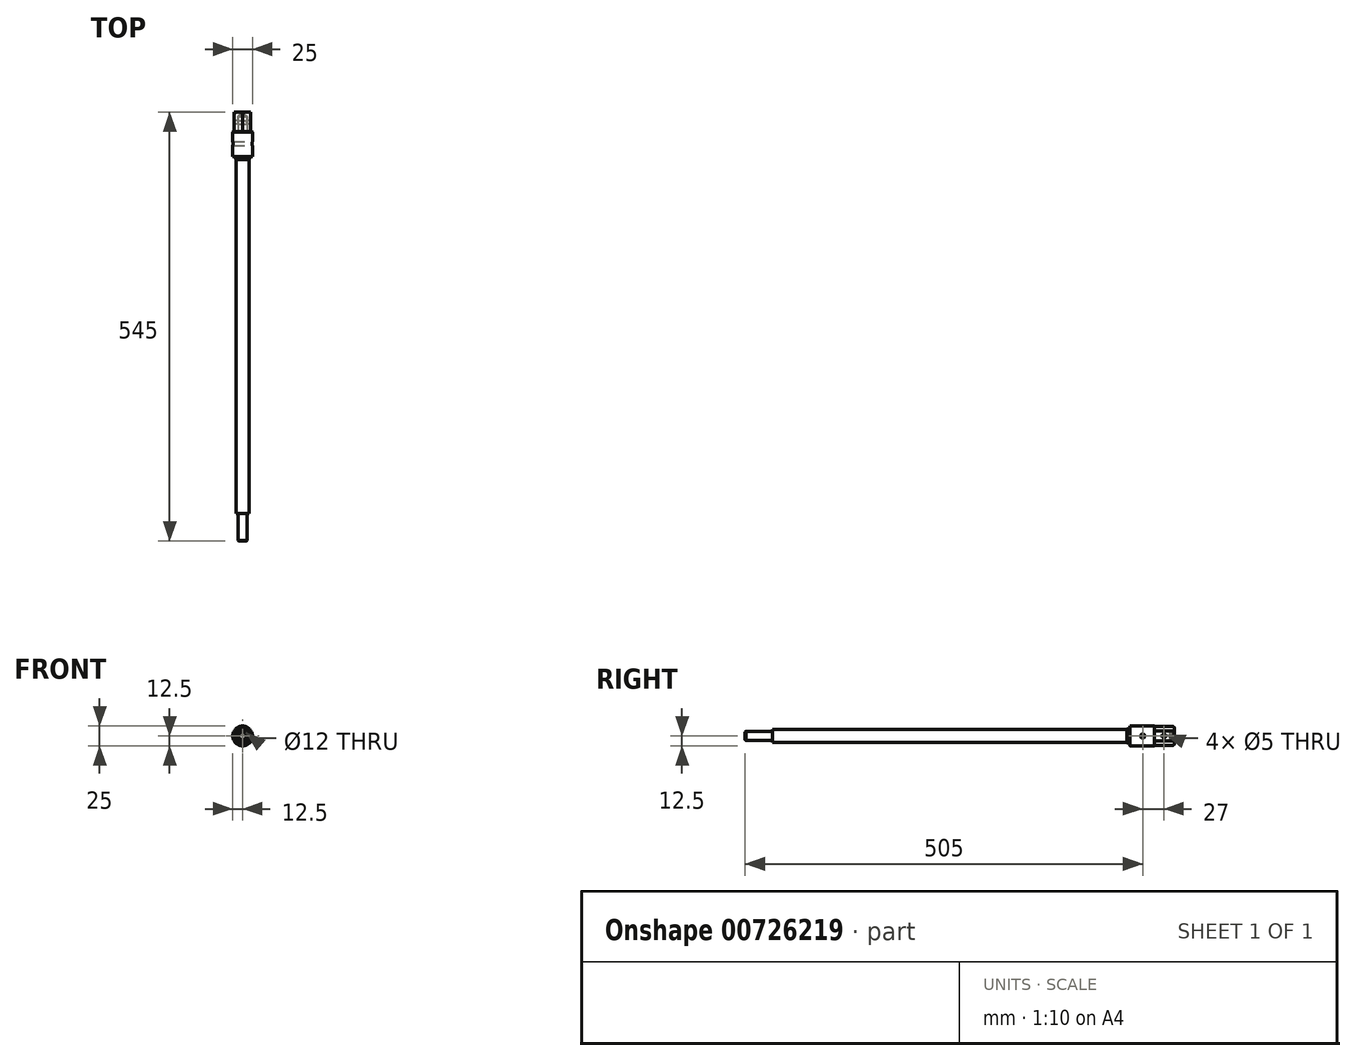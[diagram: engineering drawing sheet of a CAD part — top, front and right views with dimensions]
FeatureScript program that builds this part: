
annotation { "Feature Type Name" : "Feature", "Feature Type Description" : "" }
export const myFeature = defineFeature(function(context is Context, id is Id, definition is map)
    precondition{}
    {
        {
            var Q0;
            Q0=qCreatedBy(makeId("Front.planeOp"),FACE);
            var sketch = newSketch(context, id + "F0", { "sketchPlane" : qUnion([Q0])});
            skCircle(sketch, "E0.cCircle", {"center": v(0, 0) * mm, "radius": 10.5 * mm, "construction": true});
            skLineSegment(sketch, "E0.0", {"start": v(0, 12.12) * mm, "end": v(10.5, 6.06) * mm});
            skLineSegment(sketch, "E0.1", {"start": v(10.5, 6.06) * mm, "end": v(10.5, -6.06) * mm});
            skLineSegment(sketch, "E0.2", {"start": v(10.5, -6.06) * mm, "end": v(0, -12.12) * mm});
            skLineSegment(sketch, "E0.3", {"start": v(0, -12.12) * mm, "end": v(-10.5, -6.06) * mm});
            skLineSegment(sketch, "E0.4", {"start": v(-10.5, -6.06) * mm, "end": v(-10.5, 6.06) * mm});
            skLineSegment(sketch, "E0.5", {"start": v(-10.5, 6.06) * mm, "end": v(0, 12.12) * mm});
            skPoint(sketch, "E0.0.midPoint", {"position": v(5.25, 9.1) * mm});
            skSolve(sketch);
        }
        {
            var Q0;
            Q0 = qSketchRegion(id + "F0", true);
            extrude(context, id + "F1", {"entities" : qUnion([Q0]), "depth" : 25 * mm, "offsetDistance" : 25 * mm});
        }
        {
            var Q0;
            Q0=qCreatedBy(makeId("Right.planeOp"),FACE);
            var sketch = newSketch(context, id + "F2", { "sketchPlane" : qUnion([Q0])});
            skLineSegment(sketch, "E1", {"start": v(0, 12.12) * mm, "end": v(-1.5, 12.12) * mm});
            skLineSegment(sketch, "E2", {"start": v(-1.5, 12.12) * mm, "end": v(0, 10.62) * mm});
            skLineSegment(sketch, "E3", {"start": v(0, 10.62) * mm, "end": v(0, 12.12) * mm});
            skLineSegment(sketch, "E4", {"start": v(0, 0) * mm, "end": v(-6.38, 0) * mm, "construction": true});
            skSolve(sketch);
        }
        {
            var Q0;
            Q0 = qSketchRegion(id + "F2", true);
            var Q1;
            Q1=sQuery(id+"F2.wireOp",EDGE,"E4");
            revolve(context, id + "F3", {"operationType" : NewBodyOperationType.REMOVE, "entities" : qUnion([Q0]), "axis" : qUnion([Q1]), "revolveType" : RevolveType.FULL});
        }
        {
            var Q0;
            Q0=makeQuery(id+"F1.opExtrude","CAP_FACE",FACE,{"disambiguationData":[OSD([sQuery(id+"F0.wireOp",EDGE,"E0.0"),sQuery(id+"F0.wireOp",EDGE,"E0.1"),sQuery(id+"F0.wireOp",EDGE,"E0.2"),sQuery(id+"F0.wireOp",EDGE,"E0.3"),sQuery(id+"F0.wireOp",EDGE,"E0.4"),sQuery(id+"F0.wireOp",EDGE,"E0.5")])],"isStart":false});
            var sketch = newSketch(context, id + "F4", { "sketchPlane" : qUnion([Q0])});
            skPoint(sketch, "E5", {"position": v(0, 0) * mm});
            skSolve(sketch);
        }
        {
            var Q0;
            Q0=sQuery(id+"F4.wireOp",VERTEX,"E5");
            var Q1;
            Q1=makeQuery(id+"F1.opExtrude","SWEPT_BODY",BODY,{"disambiguationData":[OSD([sQuery(id+"F0.wireOp",EDGE,"E0.0"),sQuery(id+"F0.wireOp",EDGE,"E0.1"),sQuery(id+"F0.wireOp",EDGE,"E0.2"),sQuery(id+"F0.wireOp",EDGE,"E0.3"),sQuery(id+"F0.wireOp",EDGE,"E0.4"),sQuery(id+"F0.wireOp",EDGE,"E0.5")])]});
            hole(context, id + "F5", {"style" : HoleStyle.SIMPLE, "endStyle" : HoleEndStyle.BLIND, "holeDiameter" : 12 * mm, "holeDepth" : 20 * mm, "tappedDepth" : 10 * mm, "tapClearance" : 2, "locations" : qUnion([Q0]), "scope" : qUnion([Q1]), "majorDiameter" : 5 * mm, "startStyle" : HoleStartStyle.PART});
        }
        {
            var Q0;
            Q0=makeQuery(id+"F1.opExtrude","SWEPT_FACE",FACE,{"disambiguationData":[OSD([sQuery(id+"F0.wireOp",EDGE,"E0.1")])]});
            var sketch = newSketch(context, id + "F6", { "sketchPlane" : qUnion([Q0])});
            skPoint(sketch, "E6", {"position": v(-13, 0) * mm});
            skSolve(sketch);
        }
        {
            var Q0;
            Q0=sQuery(id+"F6.wireOp",VERTEX,"61b6d332-a3a9-4a86-aea2-c6c1109fe6f7");
            var Q1;
            Q1=sQuery(id+"F6.wireOp",VERTEX,"E6");
            var Q2;
            Q2=makeQuery(id+"F1.opExtrude","SWEPT_BODY",BODY,{"disambiguationData":[OSD([sQuery(id+"F0.wireOp",EDGE,"E0.0"),sQuery(id+"F0.wireOp",EDGE,"E0.1"),sQuery(id+"F0.wireOp",EDGE,"E0.2"),sQuery(id+"F0.wireOp",EDGE,"E0.3"),sQuery(id+"F0.wireOp",EDGE,"E0.4"),sQuery(id+"F0.wireOp",EDGE,"E0.5")])]});
            hole(context, id + "F7", {"style" : HoleStyle.SIMPLE, "endStyle" : HoleEndStyle.THROUGH, "standardTappedOrClearance" : lookupTablePath({ "standard" : "ISO", "size" : "5", "type" : "Drilled" }), "standardBlindInLast" : lookupTablePath({ "standard" : "ISO", "size" : "5", "type" : "Drilled" }), "holeDiameter" : 5 * mm, "tappedDepth" : 10 * mm, "tapClearance" : 2, "locations" : qUnion([Q0, Q1]), "scope" : qUnion([Q2]), "majorDiameter" : 5 * mm, "startStyle" : HoleStartStyle.PART});
        }
        {
            var Q0;
            Q0=makeQuery(id+"F1.opExtrude","CAP_FACE",FACE,{"disambiguationData":[OSD([sQuery(id+"F0.wireOp",EDGE,"E0.0"),sQuery(id+"F0.wireOp",EDGE,"E0.1"),sQuery(id+"F0.wireOp",EDGE,"E0.2"),sQuery(id+"F0.wireOp",EDGE,"E0.3"),sQuery(id+"F0.wireOp",EDGE,"E0.4"),sQuery(id+"F0.wireOp",EDGE,"E0.5")])],"isStart":false});
            var sketch = newSketch(context, id + "F8", { "sketchPlane" : qUnion([Q0])});
            skCircle(sketch, "E7", {"center": v(0, 0) * mm, "radius": 12.5 * mm});
            skCircle(sketch, "E8", {"center": v(0, 0) * mm, "radius": 6 * mm});
            skSolve(sketch);
        }
        {
            var Q0;
            Q0 = qSketchRegion(id + "F8", true);
            extrude(context, id + "F9", {"entities" : qUnion([Q0]), "depth" : 35 * mm, "offsetDistance" : 25 * mm});
        }
        {
            var Q0;
            Q0=makeQuery(id+"F9.opExtrude","CAP_FACE",FACE,{"disambiguationData":[OSD([sQuery(id+"F8.wireOp",EDGE,"E7"),sQuery(id+"F8.wireOp",EDGE,"E8")])],"isStart":false});
            var sketch = newSketch(context, id + "F10", { "sketchPlane" : qUnion([Q0])});
            skCircle(sketch, "E9", {"center": v(0, 0) * mm, "radius": 6 * mm});
            skSolve(sketch);
        }
        {
            var Q0;
            Q0 = qSketchRegion(id + "F10", true);
            extrude(context, id + "F11", {"entities" : qUnion([Q0]), "oppositeDirection" : true, "depth" : 54 * mm, "offsetDistance" : 25 * mm});
        }
        {
            var Q0;
            Q0=makeQuery(id+"F11.opExtrude","CAP_FACE",FACE,{"disambiguationData":[OSD([sQuery(id+"F10.wireOp",EDGE,"E9")])],"isStart":true});
            var sketch = newSketch(context, id + "F12", { "sketchPlane" : qUnion([Q0])});
            skCircle(sketch, "E10", {"center": v(0, 0) * mm, "radius": 8 * mm});
            skSolve(sketch);
        }
        {
            var Q0;
            Q0 = qSketchRegion(id + "F12", true);
            extrude(context, id + "F13", {"entities" : qUnion([Q0]), "operationType" : NewBodyOperationType.ADD, "depth" : 450 * mm, "offsetDistance" : 25 * mm});
        }
        {
            var Q0;
            Q0=makeQuery(id+"F13.opExtrude","CAP_FACE",FACE,{"disambiguationData":[OSD([sQuery(id+"F12.wireOp",EDGE,"E10")])],"isStart":false});
            var sketch = newSketch(context, id + "F14", { "sketchPlane" : qUnion([Q0]), "disableImprinting" : false});
            skCircle(sketch, "E11", {"center": v(0, 0) * mm, "radius": 6 * mm});
            skSolve(sketch);
        }
        {
            var Q0;
            Q0 = qSketchRegion(id + "F14", true);
            extrude(context, id + "F15", {"entities" : qUnion([Q0]), "operationType" : NewBodyOperationType.ADD, "depth" : 35 * mm, "offsetDistance" : 25 * mm});
        }
        {
            var Q0;
            Q0=makeQuery(id+"F15.opExtrude","CAP_EDGE",EDGE,{"disambiguationData":[OSD([sQuery(id+"F14.wireOp",EDGE,"E11")])],"isStart":false});
            chamfer(context, id + "F16", {"entities" : qUnion([Q0]), "width" : 1 * mm, "tangentPropagation" : true});
        }
        {
            var Q0;
            Q0=qCreatedBy(makeId("Right.planeOp"),FACE);
            var sketch = newSketch(context, id + "F17", { "sketchPlane" : qUnion([Q0])});
            skCircle(sketch, "E12", {"center": v(-40, 0) * mm, "radius": 2.5 * mm});
            skSolve(sketch);
        }
        {
            var Q0;
            Q0 = qSketchRegion(id + "F17", true);
            extrude(context, id + "F18", {"entities" : qUnion([Q0]), "operationType" : NewBodyOperationType.REMOVE, "oppositeDirection" : true, "depth" : 25 * mm, "offsetDistance" : 25 * mm, "symmetric" : true});
        }
        {
            var Q0;
            Q0=qCreatedBy(makeId("Right.planeOp"),FACE);
            var sketch = newSketch(context, id + "F19", { "sketchPlane" : qUnion([Q0])});
            skCircle(sketch, "E13", {"center": v(-40, 0) * mm, "radius": 2.5 * mm});
            skCircle(sketch, "E14", {"center": v(-13, 0) * mm, "radius": 2.5 * mm});
            skSolve(sketch);
        }
        {
            var Q0;
            Q0 = qSketchRegion(id + "F19", true);
            extrude(context, id + "F20", {"entities" : qUnion([Q0]), "operationType" : NewBodyOperationType.REMOVE, "oppositeDirection" : true, "depth" : 25 * mm, "offsetDistance" : 25 * mm, "symmetric" : true});
        }
        {
            var Q0;
            Q0=makeQuery(id+"F9.opExtrude","CAP_FACE",FACE,{"disambiguationData":[OSD([sQuery(id+"F8.wireOp",EDGE,"E7"),sQuery(id+"F8.wireOp",EDGE,"E8")])],"isStart":false});
            var sketch = newSketch(context, id + "F21", { "sketchPlane" : qUnion([Q0])});
            skCircle(sketch, "E15", {"center": v(0, 0) * mm, "radius": 8.62 * mm});
            skSolve(sketch);
        }
        {
            var Q0;
            Q0=makeQuery(id+"F21.imprint","IMPRINT",FACE,{"disambiguationData":[TD([[makeQuery(id+"F21.imprint","IMPRINT",EDGE,{"derivedFrom":sQuery(id+"F21.wireOp",EDGE,"E15")}),-1.0]])]});
            extrude(context, id + "F22", {"entities" : qUnion([Q0]), "operationType" : NewBodyOperationType.REMOVE, "oppositeDirection" : true, "depth" : 3.5 * mm, "offsetDistance" : 25 * mm});
        }
        {
            var Q0;
            Q0=makeQuery(id+"F9.opExtrude","CAP_FACE",FACE,{"disambiguationData":[OSD([sQuery(id+"F8.wireOp",EDGE,"E7"),sQuery(id+"F8.wireOp",EDGE,"E8")])],"isStart":false});
            var Q1;
            Q1=makeQuery(id+"F9.opExtrude","SWEPT_FACE",FACE,{"disambiguationData":[OSD([sQuery(id+"F8.wireOp",EDGE,"E7")])]});
            chamfer(context, id + "F23", {"entities" : qUnion([Q0, Q1]), "width" : .25 * mm, "tangentPropagation" : true});
        }
    });
